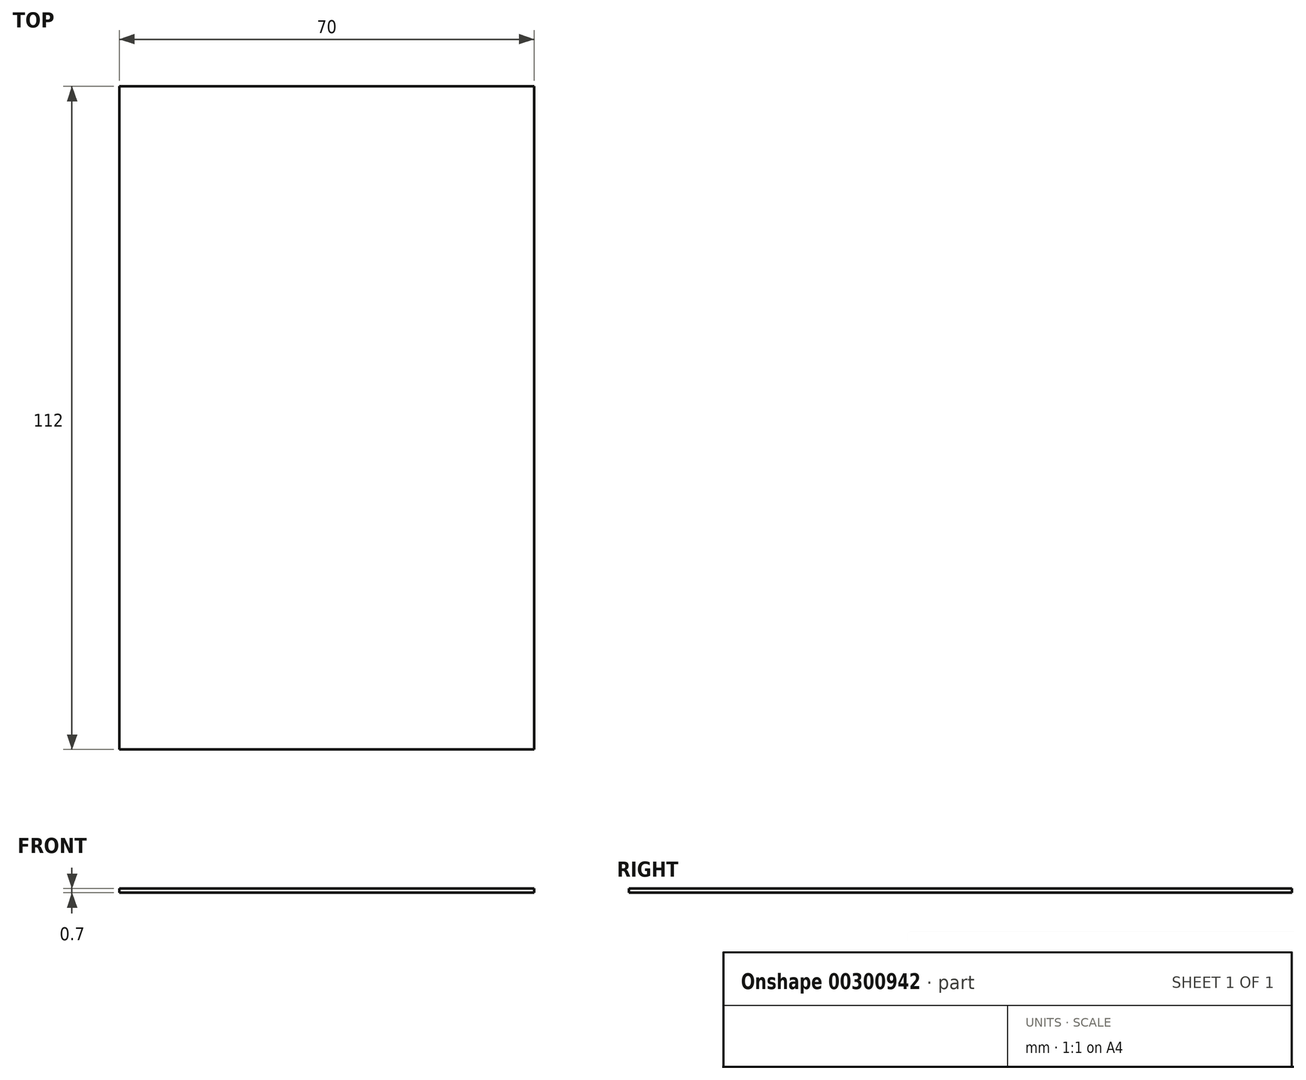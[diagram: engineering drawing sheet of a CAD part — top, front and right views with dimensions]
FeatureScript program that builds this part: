
annotation { "Feature Type Name" : "Feature", "Feature Type Description" : "" }
export const myFeature = defineFeature(function(context is Context, id is Id, definition is map)
    precondition{}
    {
        {
            var Q0;
            Q0=qCreatedBy(makeId("Top.planeOp"),FACE);
            var sketch = newSketch(context, id + "F0", { "sketchPlane" : qUnion([Q0])});
            skLineSegment(sketch, "E0", {"start": v(0, 0) * mm, "end": v(1000, 0) * mm});
            skLineSegment(sketch, "E1", {"start": v(1000, 0) * mm, "end": v(1000, 1600) * mm});
            skLineSegment(sketch, "E2", {"start": v(1000, 1600) * mm, "end": v(0, 1600) * mm});
            skLineSegment(sketch, "E3", {"start": v(0, 1600) * mm, "end": v(0, 0) * mm});
            skSolve(sketch);
        }
        {
            var Q0;
            Q0=makeQuery(id+"F0.imprint","IMPRINT",FACE,{"disambiguationData":[TD([[makeQuery(id+"F0.imprint","IMPRINT",EDGE,{"derivedFrom":sQuery(id+"F0.wireOp",EDGE,"E0")}),1.0]])]});
            extrude(context, id + "F1", {"entities" : qUnion([Q0]), "oppositeDirection" : true, "depth" : 10 * mm});
        }
        {
            var Q0;
            Q0=makeQuery(id+"F1.opExtrude","SWEPT_BODY",BODY,{"disambiguationData":[OSD([sQuery(id+"F0.wireOp",EDGE,"E0"),sQuery(id+"F0.wireOp",EDGE,"E1"),sQuery(id+"F0.wireOp",EDGE,"E2"),sQuery(id+"F0.wireOp",EDGE,"E3")])]});
            var Q1;
            Q1=qCreatedBy(makeId("Origin.pointOp"),VERTEX);
            var Q2;
            Q2=qCreatedBy(makeId("Origin.pointOp"),VERTEX);
            transform(context, id + "F2", {"entities" : qUnion([Q0]), "transformType" : TransformType.SCALE_UNIFORMLY, "scale" : 0.07, "scalePoint" : qUnion([Q2]), "makeCopy" : false});
        }
    });
